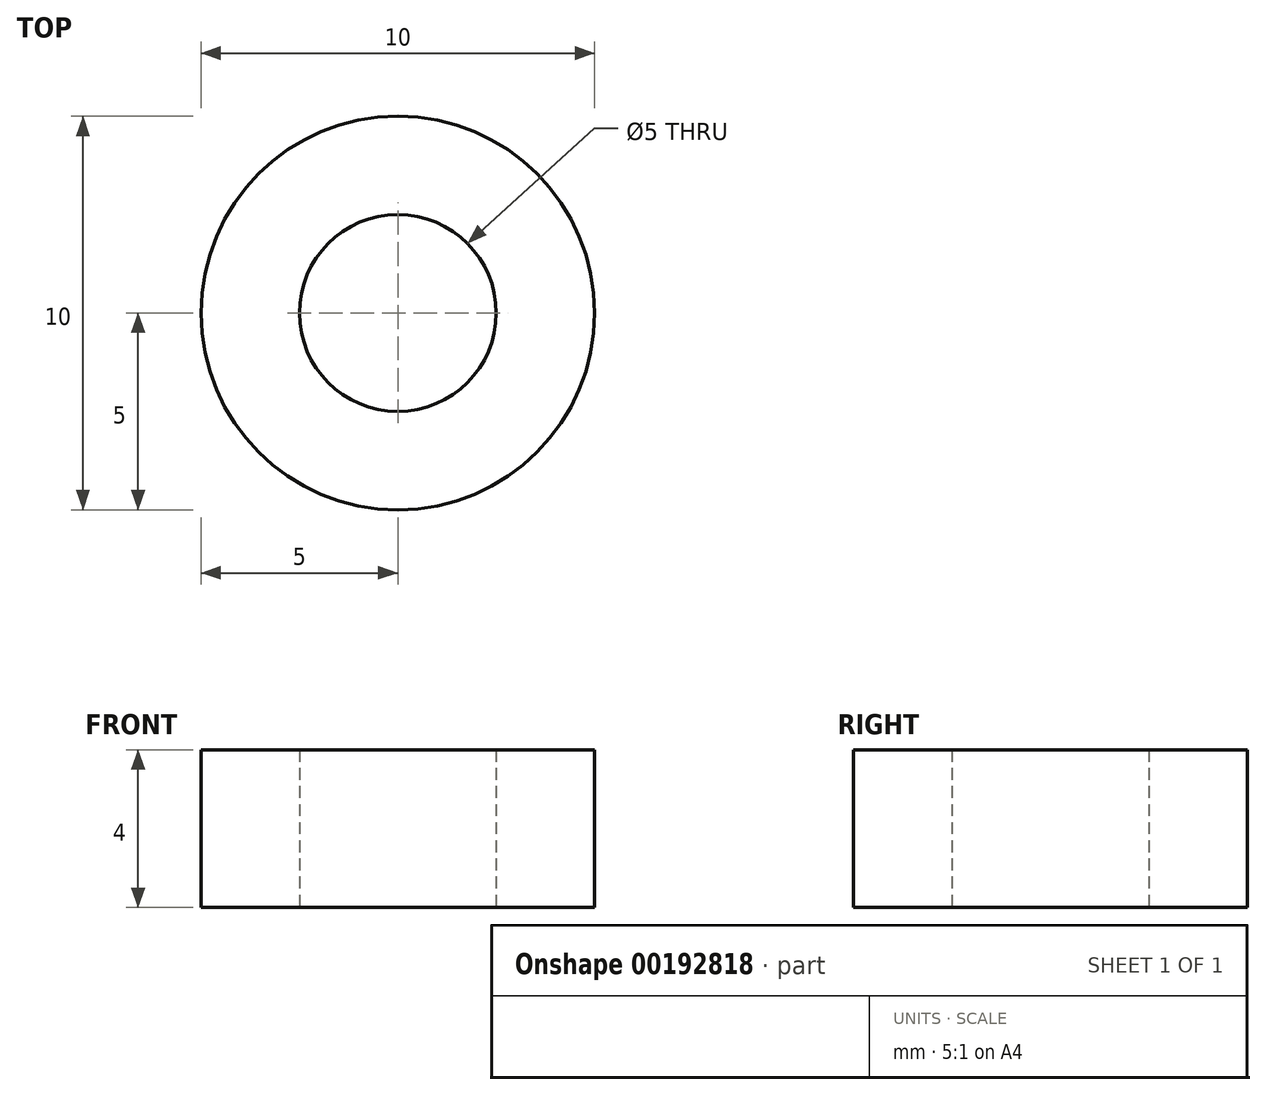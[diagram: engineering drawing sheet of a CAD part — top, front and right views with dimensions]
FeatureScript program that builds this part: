
annotation { "Feature Type Name" : "Feature", "Feature Type Description" : "" }
export const myFeature = defineFeature(function(context is Context, id is Id, definition is map)
    precondition{}
    {
        {
            var Q0;
            Q0=qCreatedBy(makeId("Top.planeOp"),FACE);
            var sketch = newSketch(context, id + "F0", { "sketchPlane" : qUnion([Q0])});
            skCircle(sketch, "E0", {"center": v(0, 0) * mm, "radius": 5 * mm});
            skCircle(sketch, "E1", {"center": v(0, 0) * mm, "radius": 2.5 * mm});
            skSolve(sketch);
        }
        {
            var Q0;
            Q0 = qSketchRegion(id + "F0", true);
            extrude(context, id + "F1", {"entities" : qUnion([Q0]), "depth" : 4 * mm});
        }
    });
